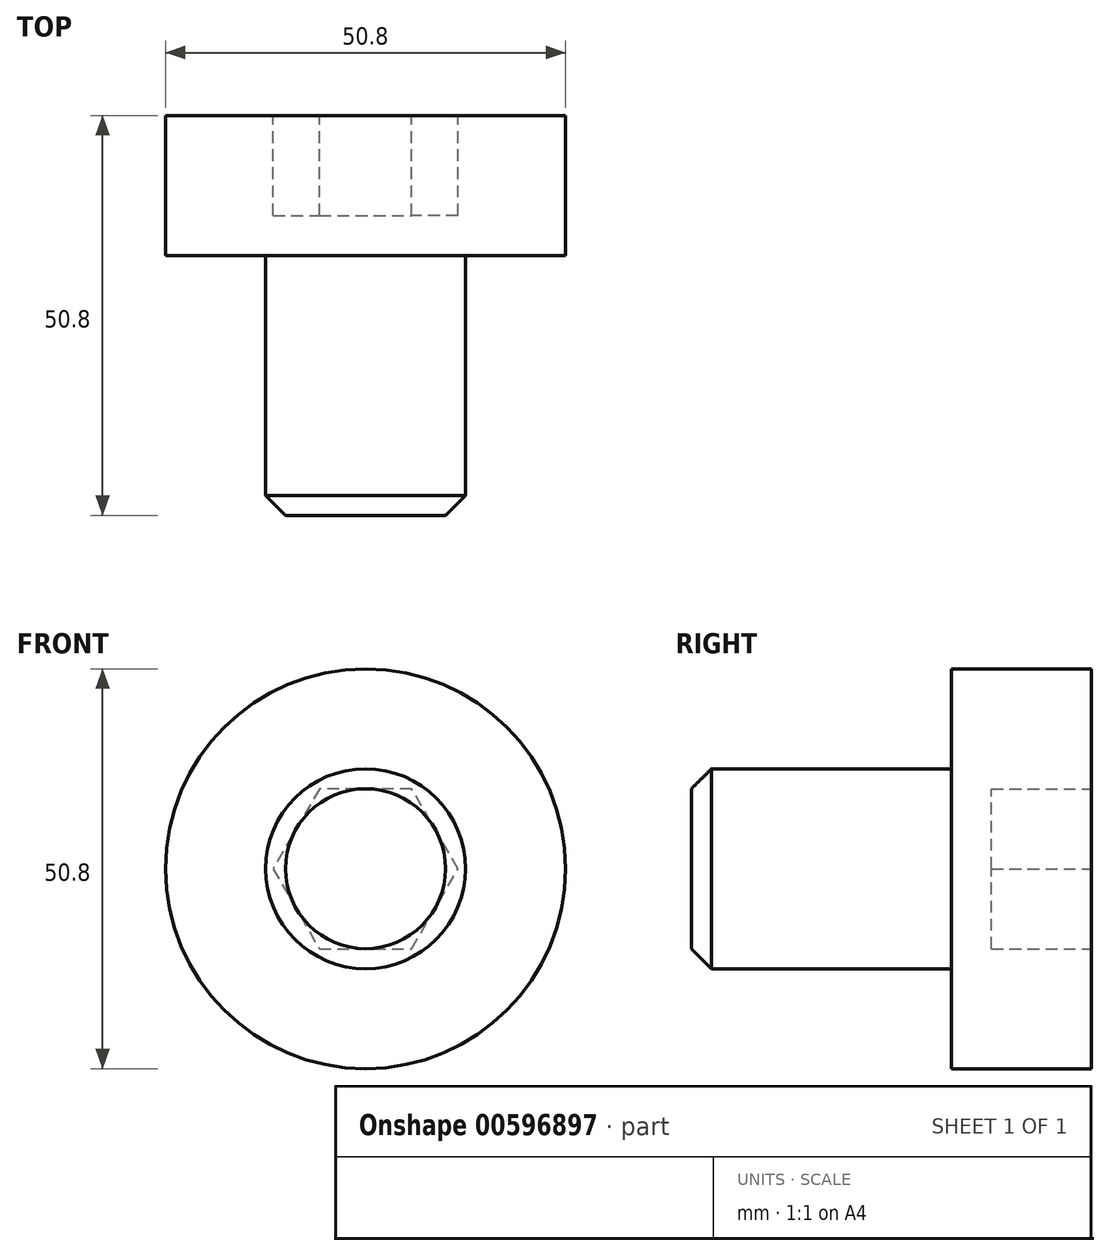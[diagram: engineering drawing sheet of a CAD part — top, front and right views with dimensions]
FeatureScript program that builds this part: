
annotation { "Feature Type Name" : "Feature", "Feature Type Description" : "" }
export const myFeature = defineFeature(function(context is Context, id is Id, definition is map)
    precondition{}
    {
        {
            var Q0;
            Q0=qCreatedBy(makeId("Top.planeOp"),FACE);
            var sketch = newSketch(context, id + "F0", { "sketchPlane" : qUnion([Q0])});
            skLineSegment(sketch, "E0", {"start": v(0, 0) * mm, "end": v(0, 50.8) * mm});
            skLineSegment(sketch, "E1", {"start": v(0, 50.8) * mm, "end": v(25.4, 50.8) * mm});
            skLineSegment(sketch, "E2", {"start": v(25.4, 50.8) * mm, "end": v(25.4, 33.02) * mm});
            skLineSegment(sketch, "E3", {"start": v(25.4, 33.02) * mm, "end": v(12.7, 33.02) * mm});
            skLineSegment(sketch, "E4", {"start": v(12.7, 33.02) * mm, "end": v(12.7, 0) * mm});
            skLineSegment(sketch, "E5", {"start": v(12.7, 0) * mm, "end": v(0, 0) * mm});
            skSolve(sketch);
        }
        {
            var Q0;
            Q0 = qSketchRegion(id + "F0", true);
            var Q1;
            Q1=sQuery(id+"F0.wireOp",EDGE,"E0");
            var Q2;
            Q2=sQuery(id+"F0.wireOp",EDGE,"E0");
            revolve(context, id + "F1", {"entities" : qUnion([Q0]), "surfaceEntities" : qUnion([Q1]), "axis" : qUnion([Q2]), "revolveType" : RevolveType.FULL});
        }
        {
            var Q0;
            Q0=makeQuery(id+"F1.opRevolve","SWEPT_EDGE",EDGE,{"disambiguationData":[OSD([sQuery(id+"F0.wireOp",EDGE,"E4"),sQuery(id+"F0.wireOp",EDGE,"E5")])]});
            chamfer(context, id + "F2", {"entities" : qUnion([Q0]), "width" : 2.54 * mm, "tangentPropagation" : true});
        }
        {
            var Q0;
            Q0=makeQuery(id+"F1.opRevolve","SWEPT_FACE",FACE,{"disambiguationData":[OSD([sQuery(id+"F0.wireOp",EDGE,"E1")])]});
            var sketch = newSketch(context, id + "F3", { "sketchPlane" : qUnion([Q0])});
            skCircle(sketch, "E6.cCircle", {"center": v(0, 0) * mm, "radius": 10.16 * mm, "construction": true});
            skLineSegment(sketch, "E6.0", {"start": v(-11.73, 0) * mm, "end": v(-5.87, 10.16) * mm});
            skLineSegment(sketch, "E6.1", {"start": v(-5.87, 10.16) * mm, "end": v(5.87, 10.16) * mm});
            skLineSegment(sketch, "E6.2", {"start": v(5.87, 10.16) * mm, "end": v(11.73, 0) * mm});
            skLineSegment(sketch, "E6.3", {"start": v(11.73, 0) * mm, "end": v(5.87, -10.16) * mm});
            skLineSegment(sketch, "E6.4", {"start": v(5.87, -10.16) * mm, "end": v(-5.87, -10.16) * mm});
            skLineSegment(sketch, "E6.5", {"start": v(-5.87, -10.16) * mm, "end": v(-11.73, 0) * mm});
            skPoint(sketch, "E6.0.midPoint", {"position": v(-8.8, 5.08) * mm});
            skSolve(sketch);
        }
        {
            var Q0;
            Q0=makeQuery(id+"F3.imprint","IMPRINT",FACE,{"disambiguationData":[TD([[makeQuery(id+"F3.imprint","IMPRINT",EDGE,{"derivedFrom":sQuery(id+"F3.wireOp",EDGE,"E6.0")}),-1.0]])]});
            extrude(context, id + "F4", {"entities" : qUnion([Q0]), "operationType" : NewBodyOperationType.REMOVE, "oppositeDirection" : true, "depth" : 12.7 * mm, "offsetDistance" : 25.4 * mm});
        }
    });
